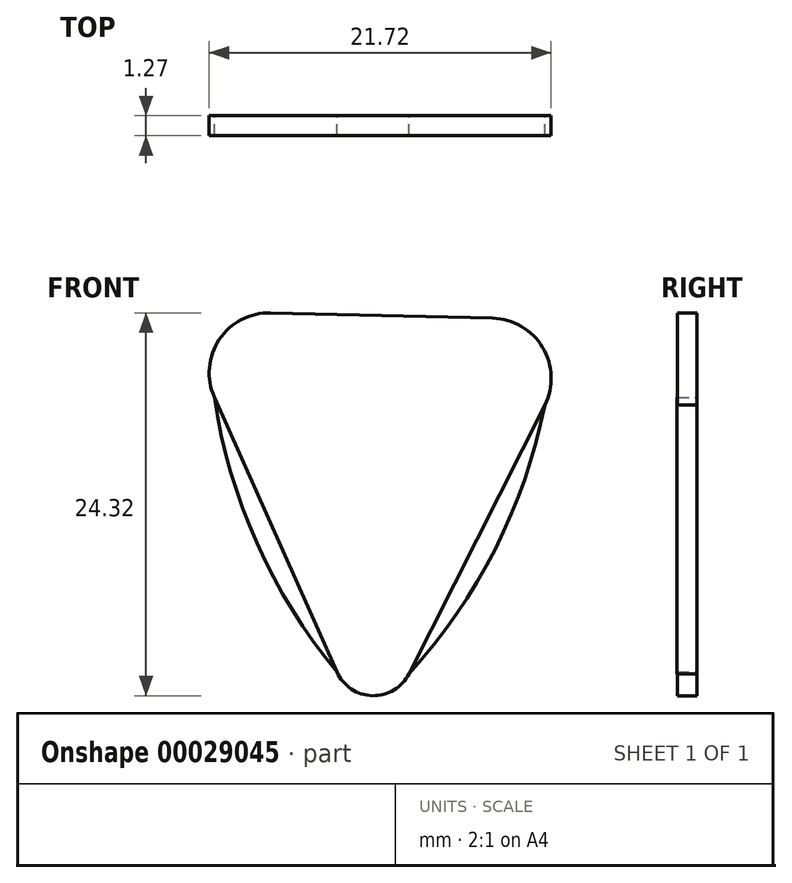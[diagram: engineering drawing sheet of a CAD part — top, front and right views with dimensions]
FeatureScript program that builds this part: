
annotation { "Feature Type Name" : "Feature", "Feature Type Description" : "" }
export const myFeature = defineFeature(function(context is Context, id is Id, definition is map)
    precondition{}
    {
        {
            var Q0;
            Q0=qCreatedBy(makeId("Front.planeOp"),FACE);
            var sketch = newSketch(context, id + "F0", { "sketchPlane" : qUnion([Q0])});
            skLineSegment(sketch, "E0", {"start": v(-9.96, 5.25) * mm, "end": v(-2.18, -12.2) * mm});
            skLineSegment(sketch, "E1", {"start": v(2.4, -12.31) * mm, "end": v(11.02, 4.74) * mm});
            skLineSegment(sketch, "E2", {"start": v(7.71, 10.27) * mm, "end": v(-6.39, 10.61) * mm});
            skPoint(sketch, "E3.visualSharp", {"position": v(13.74, 10.12) * mm});
            skArc(sketch, "E3.filletArc", {"start": v(11.02, 4.74) * mm, "mid": v(10.9, 8.42) * mm, "end": v(7.71, 10.27) * mm});
            skPoint(sketch, "E4.visualSharp", {"position": v(-12.41, 10.76) * mm});
            skArc(sketch, "E4.filletArc", {"start": v(-6.39, 10.61) * mm, "mid": v(-9.65, 8.91) * mm, "end": v(-9.96, 5.25) * mm});
            skPoint(sketch, "E5.visualSharp", {"position": v(0, -17.08) * mm});
            skArc(sketch, "E5.filletArc", {"start": v(-2.18, -12.2) * mm, "mid": v(0.08, -13.7) * mm, "end": v(2.4, -12.31) * mm});
            skArc(sketch, "E6", {"start": v(-9.96, 5.25) * mm, "mid": v(-7.26, -4) * mm, "end": v(-2.18, -12.2) * mm});
            skArc(sketch, "E7", {"start": v(2.4, -12.31) * mm, "mid": v(7.88, -4.37) * mm, "end": v(11.02, 4.74) * mm});
            skSolve(sketch);
        }
        {
            var Q0;
            Q0=makeQuery(id+"F0.imprint","IMPRINT",FACE,{"disambiguationData":[TD([[makeQuery(id+"F0.imprint","IMPRINT",EDGE,{"derivedFrom":sQuery(id+"F0.wireOp",EDGE,"E0")}),1.0]])]});
            extrude(context, id + "F1", {"entities" : qUnion([Q0]), "depth" : 1.26 * mm});
        }
        {
            var Q0;
            Q0=makeQuery(id+"F0.imprint","IMPRINT",FACE,{"disambiguationData":[TD([[makeQuery(id+"F0.imprint","IMPRINT",EDGE,{"derivedFrom":sQuery(id+"F0.wireOp",EDGE,"E0")}),-1.0]])]});
            var Q1;
            Q1=makeQuery(id+"F0.imprint","IMPRINT",FACE,{"disambiguationData":[TD([[makeQuery(id+"F0.imprint","IMPRINT",EDGE,{"derivedFrom":sQuery(id+"F0.wireOp",EDGE,"E1")}),-1.0]])]});
            extrude(context, id + "F2", {"entities" : qUnion([Q0, Q1]), "operationType" : NewBodyOperationType.ADD, "depth" : 1.27 * mm});
        }
    });
